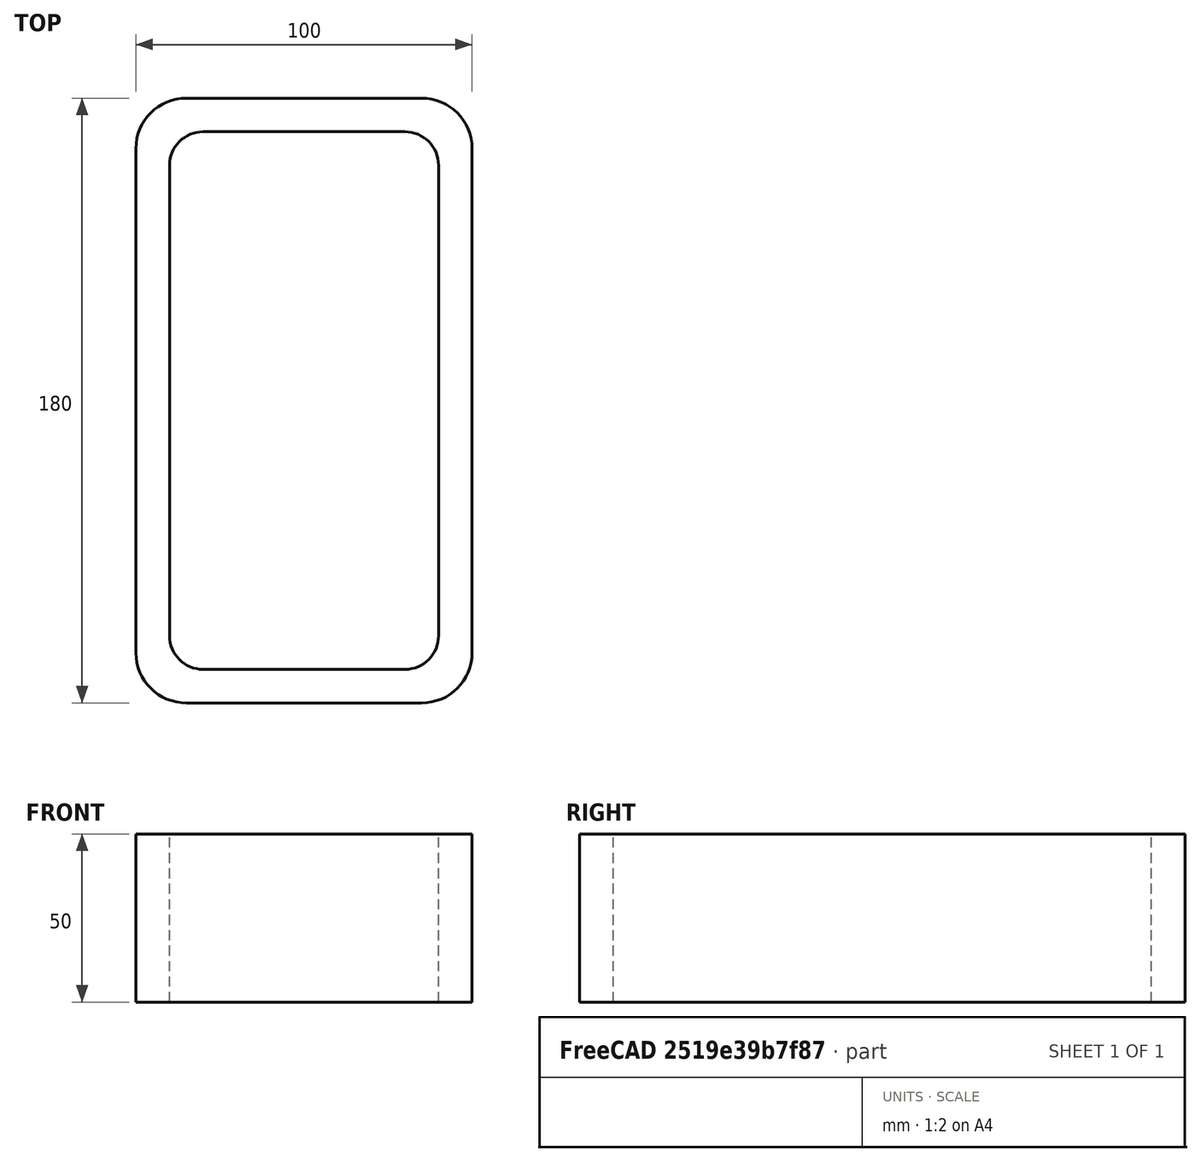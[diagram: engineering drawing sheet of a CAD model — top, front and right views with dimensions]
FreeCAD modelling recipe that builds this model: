
FCSTD DOCUMENT  (FreeCAD 0.15R4671 (Git))
Label: Rectangular hollow section 180x100x10 EN10219 S235JRH
License: All rights reserved
LicenseURL: http://en.wikipedia.org/wiki/All_rights_reserved
objects: Sketcher::SketchObject×1, Part::Extrusion×1
note: 2 computed .brp shape members not serialized (recipe doc carries the construction recipe); baked Part::Feature solids carry a one-line shape summary decoded from their .brp

FEATURE [Sketcher::SketchObject] Sketch
  sketch-geometry (16):
    g0: LineSegment StartX=-30 StartY=80 StartZ=0 EndX=30 EndY=80 EndZ=0
    g1: LineSegment StartX=40 StartY=70 StartZ=0 EndX=40 EndY=-70 EndZ=0
    g2: LineSegment StartX=30 StartY=-80 StartZ=0 EndX=-30 EndY=-80 EndZ=0
    g3: LineSegment StartX=-40 StartY=-70 StartZ=0 EndX=-40 EndY=70 EndZ=0
    g4: LineSegment StartX=-35 StartY=90 StartZ=0 EndX=35 EndY=90 EndZ=0
    g5: LineSegment StartX=50 StartY=75 StartZ=0 EndX=50 EndY=-75 EndZ=0
    g6: LineSegment StartX=35 StartY=-90 StartZ=0 EndX=-35 EndY=-90 EndZ=0
    g7: LineSegment StartX=-50 StartY=-75 StartZ=0 EndX=-50 EndY=75 EndZ=0
    g8: ArcOfCircle CenterX=-30 CenterY=70 CenterZ=0 NormalX=0 NormalY=0 NormalZ=1 Radius=10 StartAngle=1.5708 EndAngle=3.14159
    g9: ArcOfCircle CenterX=30 CenterY=70 CenterZ=0 NormalX=0 NormalY=0 NormalZ=1 Radius=10 StartAngle=0 EndAngle=1.5708
    g10: ArcOfCircle CenterX=30 CenterY=-70 CenterZ=0 NormalX=0 NormalY=0 NormalZ=1 Radius=10 StartAngle=4.71239 EndAngle=6.28319
    g11: ArcOfCircle CenterX=-30 CenterY=-70 CenterZ=0 NormalX=0 NormalY=0 NormalZ=1 Radius=10 StartAngle=3.14159 EndAngle=4.71239
    g12: ArcOfCircle CenterX=35 CenterY=75 CenterZ=0 NormalX=0 NormalY=0 NormalZ=1 Radius=15 StartAngle=0 EndAngle=1.5708
    g13: ArcOfCircle CenterX=35 CenterY=-75 CenterZ=0 NormalX=0 NormalY=0 NormalZ=1 Radius=15 StartAngle=4.71239 EndAngle=6.28319
    g14: ArcOfCircle CenterX=-35 CenterY=-75 CenterZ=0 NormalX=0 NormalY=0 NormalZ=1 Radius=15 StartAngle=3.14159 EndAngle=4.71239
    g15: ArcOfCircle CenterX=-35 CenterY=75 CenterZ=0 NormalX=0 NormalY=0 NormalZ=1 Radius=15 StartAngle=1.5708 EndAngle=3.14159
  constraints (36):
    c: Horizontal(g2)
    c: Vertical(g3)
    c: Horizontal(g6)
    c: Vertical(g7)
    c: Tangent(g3,g8) = 1.5708
    c: Tangent(g0,g8) = 1.5708
    c: Tangent(g0,g9) = 1.5708
    c: Tangent(g1,g9) = 1.5708
    c: Tangent(g1,g10) = 1.5708
    c: Tangent(g2,g10) = 1.5708
    c: Tangent(g2,g11) = 1.5708
    c: Tangent(g3,g11) = 1.5708
    c: Tangent(g4,g12) = 1.5708
    c: Tangent(g5,g12) = 1.5708
    c: Tangent(g5,g13) = 1.5708
    c: Tangent(g6,g13) = 1.5708
    c: Tangent(g6,g14) = 1.5708
    c: Tangent(g7,g14) = 1.5708
    c: Tangent(g7,g15) = 1.5708
    c: Tangent(g4,g15) = 1.5708
    c: Equal(g9,g8)
    c: Equal(g9,g11)
    c: Equal(g9,g10)
    c: Equal(g12,g15)
    c: Equal(g12,g14)
    c: Equal(g12,g13)
    c: Symmetric(g4,g6,g-1)
    c: Symmetric(g7,g5,g-2)
    c: DistanceY(g4,g6) = -180
    c: DistanceX(g7,g5) = 100
    c: Symmetric(g3,g1,g-2)
    c: Symmetric(g0,g2,g-1)
    c: DistanceY(g0,g4) = 10
    c: DistanceX(g5,g1) = -10
    c: Radius(g9) = 10
    c: Radius(g12) = 15
FEATURE [Part::Extrusion] Extrude  label="Rectangular hollow section 180x100x10 EN10219 S235JRH"
  Base = -> Sketch
  Dir = (0,0,50)
  Solid = true
